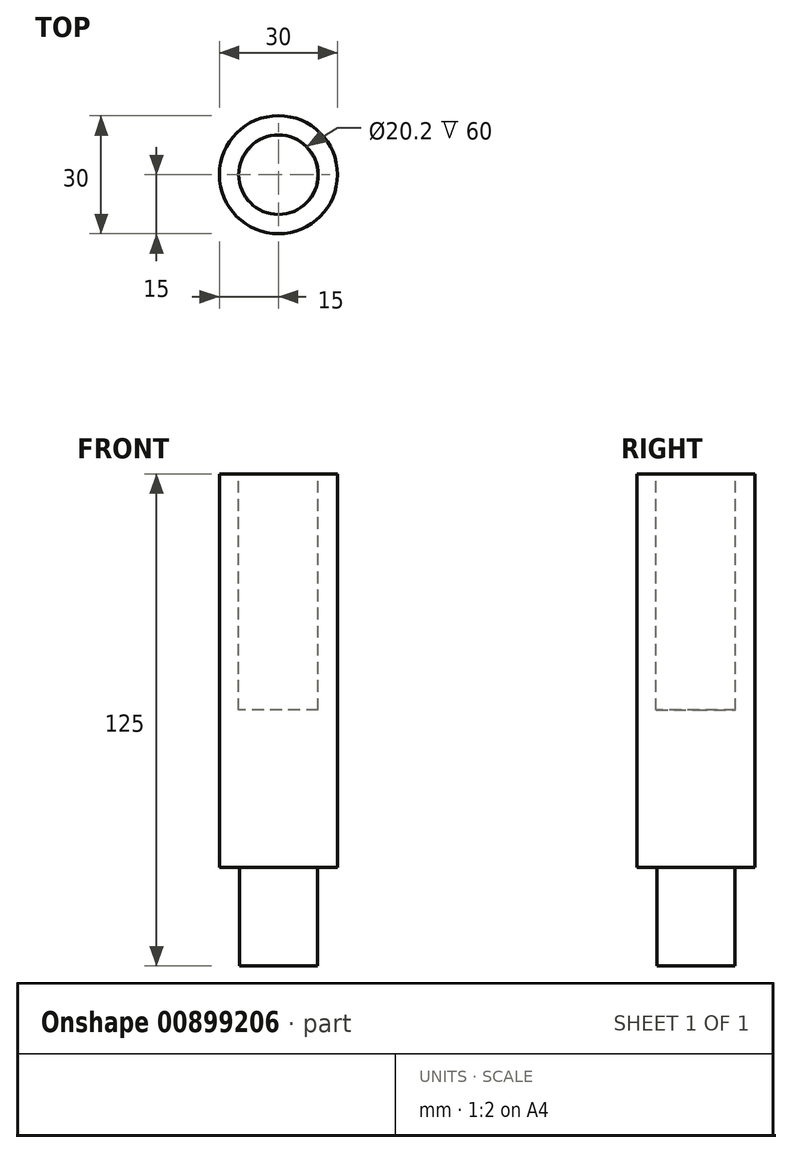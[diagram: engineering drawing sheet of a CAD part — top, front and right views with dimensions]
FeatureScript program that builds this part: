
annotation { "Feature Type Name" : "Feature", "Feature Type Description" : "" }
export const myFeature = defineFeature(function(context is Context, id is Id, definition is map)
    precondition{}
    {
        {
            var Q0;
            Q0=qCreatedBy(makeId("Front.planeOp"),FACE);
            var sketch = newSketch(context, id + "F0", { "sketchPlane" : qUnion([Q0])});
            skLineSegment(sketch, "E0", {"start": v(0, 0) * mm, "end": v(-9.9, 0) * mm});
            skLineSegment(sketch, "E1", {"start": v(-9.9, 0) * mm, "end": v(-9.9, 25) * mm});
            skLineSegment(sketch, "E2", {"start": v(-9.9, 25) * mm, "end": v(-15, 25) * mm});
            skLineSegment(sketch, "E3", {"start": v(-15, 25) * mm, "end": v(-15, 125) * mm});
            skLineSegment(sketch, "E4", {"start": v(-15, 125) * mm, "end": v(-10.1, 125) * mm});
            skLineSegment(sketch, "E5", {"start": v(-10.1, 125) * mm, "end": v(-10.1, 65) * mm});
            skLineSegment(sketch, "E6", {"start": v(-10.1, 65) * mm, "end": v(0, 65) * mm});
            skLineSegment(sketch, "E7", {"start": v(0, 65) * mm, "end": v(0, 0) * mm});
            skSolve(sketch);
        }
        {
            var Q0;
            Q0=makeQuery(id+"F0.imprint","IMPRINT",FACE,{"disambiguationData":[TD([[makeQuery(id+"F0.imprint","IMPRINT",EDGE,{"derivedFrom":sQuery(id+"F0.wireOp",EDGE,"E0")}),-1.0]])]});
            var Q1;
            Q1=sQuery(id+"F0.wireOp",EDGE,"E7");
            revolve(context, id + "F1", {"surfaceOperationType" : NewSurfaceOperationType.NEW, "entities" : qUnion([Q0]), "axis" : qUnion([Q1]), "revolveType" : RevolveType.FULL});
        }
    });
